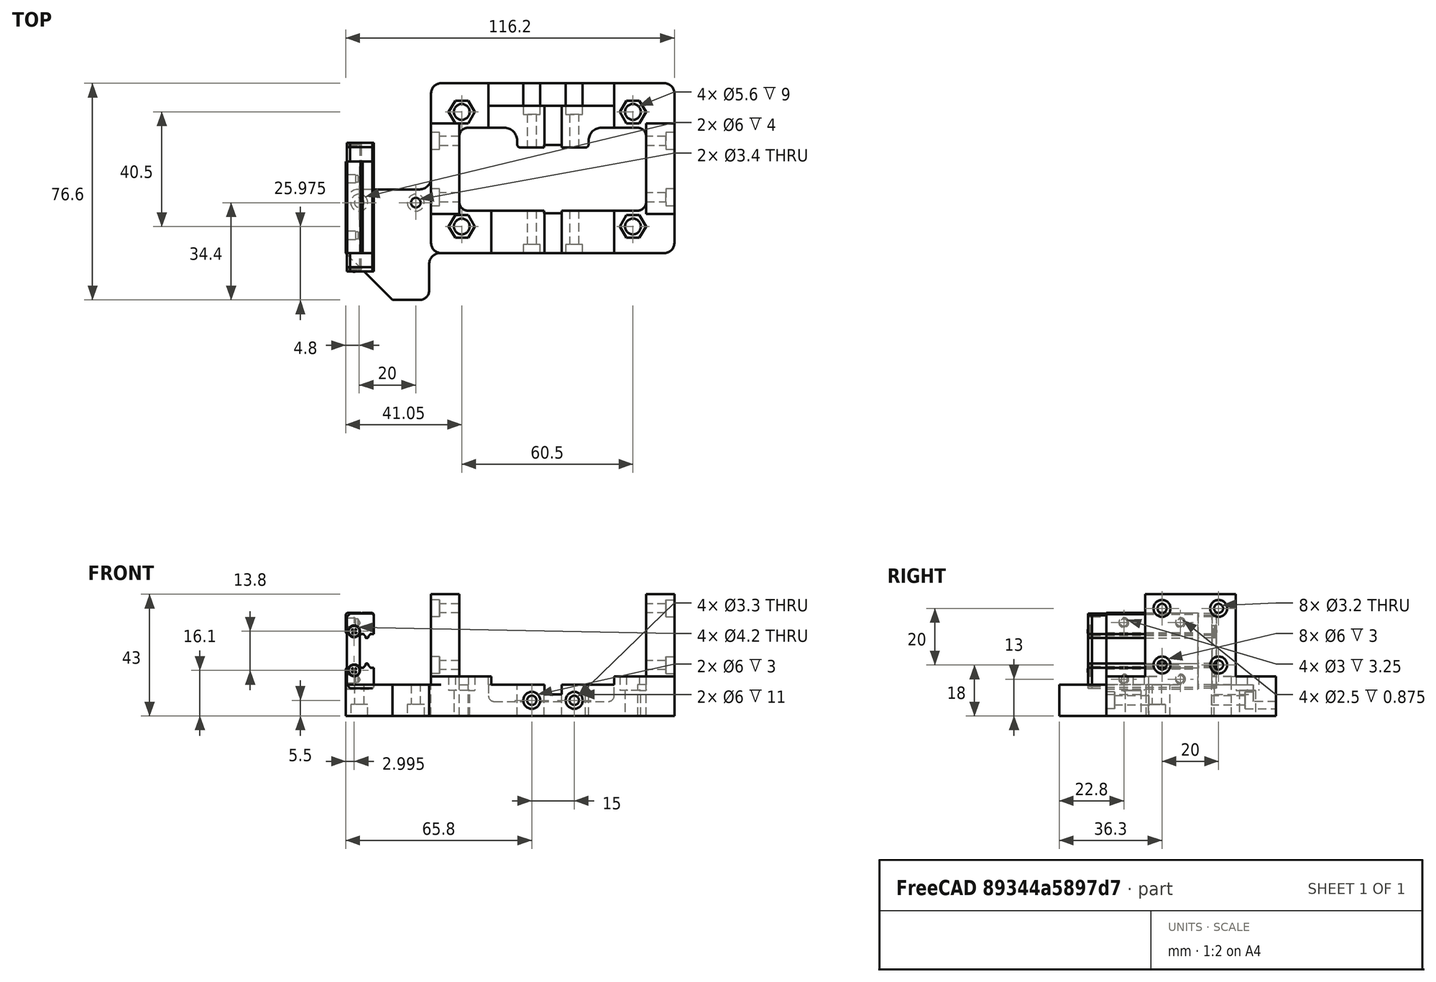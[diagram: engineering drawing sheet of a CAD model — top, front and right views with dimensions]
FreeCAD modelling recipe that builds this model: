
FCSTD DOCUMENT  (FreeCAD 0.19R24291 (Git))
Label: Carriage Mount
License: All rights reserved
LicenseURL: http://en.wikipedia.org/wiki/All_rights_reserved
objects: Sketcher::SketchObject×13, PartDesign::Pocket×10, Part::Feature×9, PartDesign::Pad×3, Mesh::Feature×2, App::Part×1, PartDesign::Body×1, Part::Fillet×1
note: 50 computed .brp shape members not serialized (recipe doc carries the construction recipe); baked Part::Feature solids carry a one-line shape summary decoded from their .brp

FEATURE [Mesh::Feature] y_axis_bed_carriage
  Placement = pos=(-82,-78.3,0) rot=(0,0,1;0rad)
FEATURE [Mesh::Feature] _a__y_belt_clip_x2  label="[a]_y_belt_clip_x2"
  Placement = pos=(-67,-7,115.5) rot=(1,0,0;4.71239rad)
FEATURE [Part::Feature] Part__Feature122  label="MGN12H, LINEAR GUIDE BLOCK v008"
  Placement = pos=(-22.7,16.2,23) rot=(0.57735,-0.57735,0.57735;2.0944rad)
  shape: bbox 4.316 x 1.614 x 4.52 mm, 16 faces (baked)
FEATURE [Part::Feature] Part__Feature121  label="MGN12H, LINEAR GUIDE BLOCK v007"
  Placement = pos=(-22.7,16.2,23) rot=(0.57735,-0.57735,0.57735;2.0944rad)
  shape: bbox 4.36 x 1.614 x 4.223 mm, 16 faces (baked)
FEATURE [Part::Feature] Part__Feature115  label="MGN12H, LINEAR GUIDE BLOCK v1"
  Placement = pos=(-22.7,16.2,23) rot=(0.57735,-0.57735,0.57735;2.0944rad)
  shape: bbox 10 x 32.4 x 27 mm, 66 faces (baked)
FEATURE [Part::Feature] Part__Feature123  label="MGN12H, LINEAR GUIDE BLOCK v009"
  Placement = pos=(-22.7,16.2,23) rot=(0.57735,-0.57735,0.57735;2.0944rad)
  shape: bbox 4.36 x 1.614 x 4.223 mm, 16 faces (baked)
FEATURE [Part::Feature] Part__Feature119  label="MGN12H, LINEAR GUIDE BLOCK v005"
  Placement = pos=(-22.7,16.2,23) rot=(0.57735,-0.57735,0.57735;2.0944rad)
  shape: bbox 9.6 x 1.5 x 26.4 mm, 42 faces (baked)
FEATURE [Part::Feature] Part__Feature120  label="MGN12H, LINEAR GUIDE BLOCK v006"
  Placement = pos=(-22.7,16.2,23) rot=(0.57735,-0.57735,0.57735;2.0944rad)
  shape: bbox 4.316 x 1.614 x 4.52 mm, 16 faces (baked)
FEATURE [Part::Feature] Part__Feature118  label="MGN12H, LINEAR GUIDE BLOCK v004"
  Placement = pos=(-22.7,16.2,23) rot=(0.57735,-0.57735,0.57735;2.0944rad)
  shape: bbox 9.6 x 1.5 x 26.4 mm, 42 faces (baked)
FEATURE [Part::Feature] Part__Feature116  label="MGN12H, LINEAR GUIDE BLOCK v002"
  Placement = pos=(-22.7,16.2,23) rot=(0.57735,-0.57735,0.57735;2.0944rad)
  shape: bbox 9.6 x 5 x 26.4 mm, 40 faces (baked)
FEATURE [Part::Feature] Part__Feature117  label="MGN12H, LINEAR GUIDE BLOCK v003"
  Placement = pos=(-22.7,16.2,23) rot=(0.57735,-0.57735,0.57735;2.0944rad)
  shape: bbox 9.6 x 5 x 26.4 mm, 40 faces (baked)
FEATURE [App::Part] MGN12H__LINEAR_GUIDE_BLOCK_v1  label="MGN12H, LINEAR GUIDE BLOCK v010"
  Group = -> [Part__Feature115,Part__Feature116,Part__Feature117,Part__Feature118,Part__Feature119,Part__Feature120,Part__Feature121,Part__Feature122,Part__Feature123]
  Origin = -> Origin028
  Placement = pos=(40.5,13.5,5) rot=(0,0,1;0rad)
FEATURE [Sketcher::SketchObject] Sketch
  FullyConstrained = true
  MapMode = 5
  Support = -> [XY_Plane]
  sketch-geometry (49):
    g0: LineSegment StartX=3.3 StartY=0 StartZ=0 EndX=82.5 EndY=0 EndZ=0
    g1: LineSegment StartX=86 StartY=3.5 StartZ=0 EndX=86 EndY=56.5 EndZ=0
    g2: LineSegment StartX=82.5 StartY=60 StartZ=0 EndX=3.5 EndY=60 EndZ=0
    g3: LineSegment StartX=0 StartY=56.5 StartZ=0 EndX=0 EndY=26.5 EndZ=0
    g4: ArcOfCircle CenterX=82.5 CenterY=3.5 CenterZ=0 NormalX=0 NormalY=0 NormalZ=1 AngleXU=0 Radius=3.5 StartAngle=4.71239 EndAngle=6.28319
    g5: ArcOfCircle CenterX=82.5 CenterY=56.5 CenterZ=0 NormalX=0 NormalY=0 NormalZ=1 AngleXU=0 Radius=3.5 StartAngle=7e-16 EndAngle=1.5708
    g6: ArcOfCircle CenterX=3.5 CenterY=56.5 CenterZ=0 NormalX=0 NormalY=0 NormalZ=1 AngleXU=0 Radius=3.5 StartAngle=1.5708 EndAngle=3.14159
    g7: ArcOfCircle CenterX=3.3 CenterY=-4 CenterZ=0 NormalX=0 NormalY=0 NormalZ=1 AngleXU=0 Radius=4 StartAngle=1.5708 EndAngle=3.14159
    g8: LineSegment StartX=-4 StartY=22.5 StartZ=0 EndX=-25.6 EndY=22.5 EndZ=0
    g9: LineSegment StartX=-30.2 StartY=17.9 StartZ=0 EndX=-30.2 EndY=0 EndZ=0
    g10: LineSegment StartX=-30.2 StartY=0 StartZ=0 EndX=-13.6 EndY=-16.6 EndZ=0
    g11: LineSegment StartX=-13.6 StartY=-16.6 StartZ=0 EndX=-4 EndY=-16.6 EndZ=0
    g12: LineSegment StartX=-0.7 StartY=-13.3 StartZ=0 EndX=-0.7 EndY=-4 EndZ=0
    g13: ArcOfCircle CenterX=-4 CenterY=-13.3 CenterZ=0 NormalX=0 NormalY=0 NormalZ=1 AngleXU=0 Radius=3.3 StartAngle=4.71239 EndAngle=6.28319
    g14: ArcOfCircle CenterX=-4 CenterY=26.5 CenterZ=0 NormalX=0 NormalY=0 NormalZ=1 AngleXU=0 Radius=4 StartAngle=4.71239 EndAngle=6.28319
    g15: ArcOfCircle CenterX=-25.6 CenterY=17.9 CenterZ=0 NormalX=0 NormalY=0 NormalZ=1 AngleXU=0 Radius=4.6 StartAngle=1.5708 EndAngle=3.14159
    g16: Circle CenterX=-25.4 CenterY=17.8 CenterZ=0 NormalX=0 NormalY=0 NormalZ=1 AngleXU=0 Radius=1.7
    g17: Circle CenterX=-5.4 CenterY=17.8 CenterZ=0 NormalX=0 NormalY=0 NormalZ=1 AngleXU=0 Radius=1.7
    g18: Circle CenterX=10.85 CenterY=9.375 CenterZ=0 NormalX=0 NormalY=0 NormalZ=1 AngleXU=0 Radius=2.8
    g19: Circle CenterX=10.85 CenterY=49.875 CenterZ=0 NormalX=0 NormalY=0 NormalZ=1 AngleXU=0 Radius=2.8
    g20: LineSegment StartX=10.85 StartY=9.375 StartZ=0 EndX=10.85 EndY=49.875 EndZ=0
    g21: Circle CenterX=71.35 CenterY=9.375 CenterZ=0 NormalX=0 NormalY=0 NormalZ=1 AngleXU=0 Radius=2.8
    g22: LineSegment StartX=10.85 StartY=9.375 StartZ=0 EndX=71.35 EndY=9.375 EndZ=0
    g23: Circle CenterX=71.35 CenterY=49.875 CenterZ=0 NormalX=0 NormalY=0 NormalZ=1 AngleXU=0 Radius=2.8
    g24: LineSegment StartX=71.35 StartY=9.375 StartZ=0 EndX=71.35 EndY=49.875 EndZ=0
    g25: LineSegment StartX=13 StartY=44.275 StartZ=0 EndX=25.9042 EndY=44.275 EndZ=0
    g26: LineSegment StartX=76 StartY=41.2768 StartZ=0 EndX=76 EndY=17.975 EndZ=0
    g27: LineSegment StartX=73 StartY=14.975 StartZ=0 EndX=46.2 EndY=14.975 EndZ=0
    g28: LineSegment StartX=10 StartY=17.9683 StartZ=0 EndX=10 EndY=41.275 EndZ=0
    g29: ArcOfCircle CenterX=13 CenterY=17.9683 CenterZ=0 NormalX=0 NormalY=0 NormalZ=1 AngleXU=0 Radius=3 StartAngle=3.14159 EndAngle=4.77911
    g30: ArcOfCircle CenterX=73 CenterY=17.975 CenterZ=0 NormalX=0 NormalY=0 NormalZ=1 AngleXU=0 Radius=3 StartAngle=4.71239 EndAngle=6.28319
    g31: ArcOfCircle CenterX=13 CenterY=41.275 CenterZ=0 NormalX=0 NormalY=0 NormalZ=1 AngleXU=0 Radius=3 StartAngle=1.5708 EndAngle=3.14159
    g32: ArcOfCircle CenterX=73 CenterY=41.2768 CenterZ=0 NormalX=0 NormalY=0 NormalZ=1 AngleXU=0 Radius=3 StartAngle=1e-15 EndAngle=1.53606
    g33: LineSegment StartX=30.4 StartY=39.7792 StartZ=0 EndX=30.4 EndY=38.475 EndZ=0
    g34: LineSegment StartX=31.6 StartY=37.275 StartZ=0 EndX=40 EndY=37.275 EndZ=0
    g35: LineSegment StartX=55.7 StartY=38.4708 StartZ=0 EndX=55.7 EndY=39.775 EndZ=0
    g36: LineSegment StartX=60.2 StartY=44.275 StartZ=0 EndX=73.1042 EndY=44.275 EndZ=0
    g37: ArcOfCircle CenterX=25.9042 CenterY=39.7792 CenterZ=0 NormalX=0 NormalY=0 NormalZ=1 AngleXU=0 Radius=4.49583 StartAngle=1e-16 EndAngle=1.5708
    g38: ArcOfCircle CenterX=60.2 CenterY=39.775 CenterZ=0 NormalX=0 NormalY=0 NormalZ=1 AngleXU=0 Radius=4.5 StartAngle=1.5708 EndAngle=3.14159
    g39: ArcOfCircle CenterX=54.5 CenterY=38.4708 CenterZ=0 NormalX=0 NormalY=0 NormalZ=1 AngleXU=0 Radius=1.2 StartAngle=4.79582 EndAngle=6.28319
    g40: ArcOfCircle CenterX=31.6 CenterY=38.475 CenterZ=0 NormalX=0 NormalY=0 NormalZ=1 AngleXU=0 Radius=1.2 StartAngle=3.14159 EndAngle=4.71239
    g41: LineSegment StartX=40 StartY=37.275 StartZ=0 EndX=40 EndY=38.175 EndZ=0
    g42: LineSegment StartX=40 StartY=38.175 StartZ=0 EndX=46.2 EndY=38.175 EndZ=0
    g43: LineSegment StartX=46.2 StartY=38.175 StartZ=0 EndX=46.2 EndY=37.275 EndZ=0
    g44: LineSegment StartX=46.2 StartY=37.275 StartZ=0 EndX=54.6 EndY=37.275 EndZ=0
    g45: LineSegment StartX=40 StartY=14.975 StartZ=0 EndX=40 EndY=14.075 EndZ=0
    g46: LineSegment StartX=40 StartY=14.075 StartZ=0 EndX=46.2 EndY=14.075 EndZ=0
    g47: LineSegment StartX=46.2 StartY=14.075 StartZ=0 EndX=46.2 EndY=14.975 EndZ=0
    g48: LineSegment StartX=40 StartY=14.975 StartZ=0 EndX=13.2 EndY=14.975 EndZ=0
  constraints (131):
    c: Horizontal(g0)
    c: Horizontal(g2)
    c: Vertical(g1)
    c: Vertical(g3)
    c: Tangent(g0,g4) = -1.5708
    c: Tangent(g1,g4) = -1.5708
    c: Tangent(g1,g5) = -1.5708
    c: Tangent(g2,g5) = -1.5708
    c: Tangent(g3,g6) = -1.5708
    c: Tangent(g2,g6) = -1.5708
    c: PointOnObject(g0,g-1)
    c: DistanceY(g-1,g2) = 60
    c: Radius(g6) = 3.5
    c: Coincident(g7,g0)
    c: Horizontal(g8)
    c: PointOnObject(g9,g-1)
    c: Vertical(g9)
    c: Coincident(g9,g10)
    c: Coincident(g10,g11)
    c: Horizontal(g11)
    c: Coincident(g12,g7)
    c: Vertical(g12)
    c: Tangent(g11,g13) = -1.5708
    c: Tangent(g12,g13) = -1.5708
    c: Tangent(g8,g14) = 1.5708
    c: Tangent(g3,g14) = 1.5708
    c: Tangent(g9,g15) = -1.5708
    c: Tangent(g8,g15) = -1.5708
    c: PointOnObject(g3,g-2)
    c: Equal(g6,g5)
    c: Equal(g5,g4)
    c: Angle(g7) = 1.5708
    c: DistanceY(g-1,g8) = 22.5
    c: DistanceX(g9,g-1) = 30.2
    c: DistanceY(g11,g-1) = 16.6
    c: DistanceX(g7,g-1) = 0.7
    c: Distance(g12) = 9.3
    c: Radius(g7) = 4
    c: DistanceX(g11,g11) = 9.6
    c: Radius(g15) = 4.6
    c: Radius(g14) = 4
    c: DistanceX(g3,g1) = 86
    c: DistanceY(g7,g-1) = 4
    c: Radius(g16) = 1.7
    c: Equal(g16,g17) = 1.7
    c: Horizontal(g16,g17)
    c: DistanceX(g17,g-1) = 5.4
    c: DistanceX(g16,g17) = 20
    c: DistanceY(g-1,g17) = 17.8
    c: Radius(g18) = 2.8
    c: DistanceX(g-1,g18) = 10.85
    c: DistanceY(g-1,g18) = 9.375
    c: Radius(g19) = 2.8
    c: Coincident(g18,g20)
    c: Coincident(g19,g20)
    c: Distance(g20) = 40.5
    c: Angle(g20) = 1.5708
    c: Radius(g21) = 2.8
    c: Coincident(g18,g22)
    c: Coincident(g21,g22)
    c: Distance(g22) = 60.5
    c: Perpendicular(g22,g20)
    c: Radius(g23) = 2.8
    c: Coincident(g21,g24)
    c: Coincident(g23,g24)
    c: Equal(g20,g24)
    c: Parallel(g24,g20)
    c: Horizontal(g25)
    c: Horizontal(g27)
    c: Vertical(g26)
    c: Vertical(g28)
    c: Tangent(g28,g29) = 1.5708
    c: Coincident(g48,g29) = 1.5708
    c: Tangent(g27,g30) = 1.5708
    c: Tangent(g26,g30) = 1.5708
    c: Tangent(g28,g31) = 1.5708
    c: Tangent(g25,g31) = 1.5708
    c: Coincident(g36,g32) = 1.5708
    c: Tangent(g26,g32) = 1.5708
    c: Equal(g29,g31)
    c: Equal(g31,g32)
    c: Equal(g32,g30)
    c: Radius(g29) = 3
    c: DistanceX(g-1,g28) = 10
    c: DistanceX(g26,g1) = 10
    c: DistanceY(g18,g48) = 5.6
    c: DistanceY(g25,g19) = 5.6
    c: Vertical(g33)
    c: Horizontal(g34)
    c: Vertical(g35)
    c: Tangent(g25,g36)
    c: Tangent(g25,g37) = 1.5708
    c: Tangent(g33,g37) = 1.5708
    c: Tangent(g35,g38) = 1.5708
    c: Tangent(g36,g38) = 1.5708
    c: Coincident(g44,g39) = -1.5708
    c: Tangent(g35,g39) = -1.5708
    c: Tangent(g33,g40) = -1.5708
    c: Tangent(g34,g40) = -1.5708
    c: Equal(g40,g39)
    c: DistanceY(g34,g25) = 7
    c: DistanceX(g28,g33) = 20.4
    c: DistanceX(g33,g35) = 25.3
    c: Radius(g40) = 1.2
    c: Equal(g33,g35)
    c: Equal(g25,g36)
    c: Radius(g38) = 4.5
    c: Vertical(g41)
    c: Coincident(g41,g42)
    c: Horizontal(g42)
    c: Coincident(g42,g43)
    c: Vertical(g43)
    c: Coincident(g34,g41)
    c: Coincident(g44,g43)
    c: Tangent(g34,g44)
    c: Equal(g34,g44)
    c: DistanceX(g42,g42) = 6.2
    c: DistanceX(g34,g34) = 8.4
    c: DistanceY(g43,g43) = 0.9
    c: Coincident(g45,g46)
    c: Horizontal(g46)
    c: Coincident(g46,g47)
    c: Vertical(g47)
    c: Vertical(g45)
    c: Equal(g42,g46)
    c: Equal(g43,g47)
    c: Coincident(g27,g47)
    c: Coincident(g48,g45)
    c: Tangent(g27,g48)
    c: Equal(g48,g27)
    c: DistanceX(g48,g48) = 26.8
FEATURE [PartDesign::Pad] Pad
  Direction = (1,1,1)
  Length = 11
  Length2 = 100
  Profile = -> Sketch
  Type = 0
FEATURE [Sketcher::SketchObject] Sketch001
  ExternalGeometry = -> [Pad]
  FullyConstrained = true
  MapMode = 5
  Placement = pos=(0,0,11) rot=(0,0,1;0rad)
  Support = -> [Pad]
  sketch-geometry (24):
    g0: LineSegment StartX=3.5 StartY=0 StartZ=0 EndX=21.3 EndY=0 EndZ=0
    g1: LineSegment StartX=21.3 StartY=0 StartZ=0 EndX=21.3 EndY=14.975 EndZ=0
    g2: LineSegment StartX=21.3 StartY=14.975 StartZ=0 EndX=12.9933 EndY=14.975 EndZ=0
    g3: LineSegment StartX=10 StartY=17.9683 StartZ=0 EndX=10 EndY=41.275 EndZ=0
    g4: LineSegment StartX=20.3 StartY=44.275 StartZ=0 EndX=20.3 EndY=60 EndZ=0
    g5: LineSegment StartX=20.3 StartY=60 StartZ=0 EndX=3.5 EndY=60 EndZ=0
    g6: LineSegment StartX=0 StartY=56.5 StartZ=0 EndX=0 EndY=3.5 EndZ=0
    g7: ArcOfCircle CenterX=12.9933 CenterY=17.9683 CenterZ=0 NormalX=0 NormalY=0 NormalZ=1 AngleXU=0 Radius=2.99333 StartAngle=3.14159 EndAngle=4.71239
    g8: ArcOfCircle CenterX=13 CenterY=41.275 CenterZ=0 NormalX=0 NormalY=0 NormalZ=1 AngleXU=0 Radius=3 StartAngle=1.5708 EndAngle=3.14159
    g9: ArcOfCircle CenterX=3.5 CenterY=56.5 CenterZ=0 NormalX=0 NormalY=0 NormalZ=1 AngleXU=0 Radius=3.5 StartAngle=1.5708 EndAngle=3.14159
    g10: LineSegment StartX=13 StartY=44.275 StartZ=0 EndX=20.3 EndY=44.275 EndZ=0
    g11: ArcOfCircle CenterX=3.5 CenterY=3.5 CenterZ=0 NormalX=0 NormalY=0 NormalZ=1 AngleXU=0 Radius=3.5 StartAngle=3.14159 EndAngle=4.71239
    g12: LineSegment StartX=64.7 StartY=0 StartZ=0 EndX=64.7 EndY=14.975 EndZ=0
    g13: LineSegment StartX=64.7 StartY=14.975 StartZ=0 EndX=73 EndY=14.975 EndZ=0
    g14: LineSegment StartX=76 StartY=17.975 StartZ=0 EndX=76 EndY=41.2768 EndZ=0
    g15: LineSegment StartX=73.0018 StartY=44.275 StartZ=0 EndX=64.7018 EndY=44.275 EndZ=0
    g16: LineSegment StartX=64.7018 StartY=44.275 StartZ=0 EndX=64.7018 EndY=60 EndZ=0
    g17: LineSegment StartX=64.7018 StartY=60 StartZ=0 EndX=82.5 EndY=60 EndZ=0
    g18: LineSegment StartX=86 StartY=56.5 StartZ=0 EndX=86 EndY=3.5 EndZ=0
    g19: LineSegment StartX=82.5 StartY=0 StartZ=0 EndX=64.7 EndY=0 EndZ=0
    g20: ArcOfCircle CenterX=73 CenterY=17.975 CenterZ=0 NormalX=0 NormalY=0 NormalZ=1 AngleXU=0 Radius=3 StartAngle=4.71239 EndAngle=6.28319
    g21: ArcOfCircle CenterX=73.0018 CenterY=41.2768 CenterZ=0 NormalX=0 NormalY=0 NormalZ=1 AngleXU=0 Radius=2.99819 StartAngle=1.1e-15 EndAngle=1.5708
    g22: ArcOfCircle CenterX=82.5 CenterY=56.5 CenterZ=0 NormalX=0 NormalY=0 NormalZ=1 AngleXU=0 Radius=3.5 StartAngle=0 EndAngle=1.5708
    g23: ArcOfCircle CenterX=82.5 CenterY=3.5 CenterZ=0 NormalX=0 NormalY=0 NormalZ=1 AngleXU=0 Radius=3.5 StartAngle=4.71239 EndAngle=6.28319
  constraints (56):
    c: PointOnObject(g0,g-1)
    c: Coincident(g0,g1)
    c: PointOnObject(g1,g-3)
    c: Vertical(g1)
    c: Coincident(g1,g2)
    c: Horizontal(g2)
    c: PointOnObject(g4,g-6)
    c: Vertical(g4)
    c: Coincident(g4,g5)
    c: Tangent(g3,g7) = 1.5708
    c: Tangent(g2,g7) = 1.5708
    c: Coincident(g3,g-4)
    c: DistanceX(g-1,g0) = 21.3
    c: Tangent(g3,g8) = 1.5708
    c: Coincident(g-5,g8) = 1.5708
    c: Tangent(g6,g9) = -1.5708
    c: Tangent(g5,g9) = -1.5708
    c: Coincident(g10,g8)
    c: Coincident(g10,g4)
    c: Horizontal(g10)
    c: DistanceX(g6,g4) = 20.3
    c: Coincident(g5,g-6)
    c: PointOnObject(g6,g-2)
    c: Coincident(g3,g-4)
    c: Tangent(g6,g11) = -1.5708
    c: Tangent(g0,g11) = -1.5708
    c: Radius(g11) = 3.5
    c: PointOnObject(g6,g-2)
    c: PointOnObject(g0,g-1)
    c: PointOnObject(g12,g-1)
    c: Vertical(g12)
    c: Coincident(g12,g13)
    c: Horizontal(g15)
    c: Coincident(g15,g16)
    c: PointOnObject(g16,g-6)
    c: Vertical(g16)
    c: Coincident(g16,g17)
    c: Vertical(g18)
    c: Coincident(g19,g12)
    c: Tangent(g13,g20) = -1.5708
    c: Tangent(g14,g20) = -1.5708
    c: Tangent(g15,g21) = -1.5708
    c: Tangent(g14,g21) = -1.5708
    c: Tangent(g17,g22) = 1.5708
    c: Tangent(g18,g22) = 1.5708
    c: Tangent(g19,g23) = 1.5708
    c: Tangent(g18,g23) = 1.5708
    c: Coincident(g18,g-10)
    c: DistanceX(g12,g18) = 21.3
    c: Horizontal(g19)
    c: Coincident(g13,g-8)
    c: Coincident(g14,g-9)
    c: Coincident(g14,g-9)
    c: PointOnObject(g15,g-7)
    c: Equal(g13,g15)
    c: Coincident(g17,g-6)
FEATURE [PartDesign::Pad] Pad001
  BaseFeature = -> Pad
  Direction = (1,1,1)
  Length = 3
  Length2 = 100
  Profile = -> Sketch001
  Type = 0
FEATURE [Sketcher::SketchObject] Sketch002
  ExternalGeometry = -> [Pad]
  FullyConstrained = true
  MapMode = 5
  Placement = pos=(0,0,14) rot=(0,0,1;0rad)
  Support = -> [Pad001]
  sketch-geometry (28):
    g0: LineSegment StartX=13.1594 StartY=5.375 StartZ=0 EndX=15.4688 EndY=9.375 EndZ=0
    g1: LineSegment StartX=15.4688 StartY=9.375 StartZ=0 EndX=13.1594 EndY=13.375 EndZ=0
    g2: LineSegment StartX=13.1594 StartY=13.375 StartZ=0 EndX=8.5406 EndY=13.375 EndZ=0
    g3: LineSegment StartX=8.5406 StartY=13.375 StartZ=0 EndX=6.2312 EndY=9.375 EndZ=0
    g4: LineSegment StartX=6.2312 StartY=9.375 StartZ=0 EndX=8.5406 EndY=5.375 EndZ=0
    g5: LineSegment StartX=8.5406 StartY=5.375 StartZ=0 EndX=13.1594 EndY=5.375 EndZ=0
    g6: Circle CenterX=10.85 CenterY=9.375 CenterZ=0 NormalX=0 NormalY=0 NormalZ=1 AngleXU=0 Radius=4.6188
    g7: LineSegment StartX=13.1594 StartY=45.875 StartZ=0 EndX=15.4688 EndY=49.875 EndZ=0
    g8: LineSegment StartX=15.4688 StartY=49.875 StartZ=0 EndX=13.1594 EndY=53.875 EndZ=0
    g9: LineSegment StartX=13.1594 StartY=53.875 StartZ=0 EndX=8.5406 EndY=53.875 EndZ=0
    g10: LineSegment StartX=8.5406 StartY=53.875 StartZ=0 EndX=6.2312 EndY=49.875 EndZ=0
    g11: LineSegment StartX=6.2312 StartY=49.875 StartZ=0 EndX=8.5406 EndY=45.875 EndZ=0
    g12: LineSegment StartX=8.5406 StartY=45.875 StartZ=0 EndX=13.1594 EndY=45.875 EndZ=0
    g13: Circle CenterX=10.85 CenterY=49.875 CenterZ=0 NormalX=0 NormalY=0 NormalZ=1 AngleXU=0 Radius=4.6188
    g14: LineSegment StartX=73.6594 StartY=45.875 StartZ=0 EndX=75.9688 EndY=49.875 EndZ=0
    g15: LineSegment StartX=75.9688 StartY=49.875 StartZ=0 EndX=73.6594 EndY=53.875 EndZ=0
    g16: LineSegment StartX=73.6594 StartY=53.875 StartZ=0 EndX=69.0406 EndY=53.875 EndZ=0
    g17: LineSegment StartX=69.0406 StartY=53.875 StartZ=0 EndX=66.7312 EndY=49.875 EndZ=0
    g18: LineSegment StartX=66.7312 StartY=49.875 StartZ=0 EndX=69.0406 EndY=45.875 EndZ=0
    g19: LineSegment StartX=69.0406 StartY=45.875 StartZ=0 EndX=73.6594 EndY=45.875 EndZ=0
    g20: Circle CenterX=71.35 CenterY=49.875 CenterZ=0 NormalX=0 NormalY=0 NormalZ=1 AngleXU=0 Radius=4.6188
    g21: LineSegment StartX=73.6594 StartY=5.375 StartZ=0 EndX=75.9688 EndY=9.375 EndZ=0
    g22: LineSegment StartX=75.9688 StartY=9.375 StartZ=0 EndX=73.6594 EndY=13.375 EndZ=0
    g23: LineSegment StartX=73.6594 StartY=13.375 StartZ=0 EndX=69.0406 EndY=13.375 EndZ=0
    g24: LineSegment StartX=69.0406 StartY=13.375 StartZ=0 EndX=66.7312 EndY=9.375 EndZ=0
    g25: LineSegment StartX=66.7312 StartY=9.375 StartZ=0 EndX=69.0406 EndY=5.375 EndZ=0
    g26: LineSegment StartX=69.0406 StartY=5.375 StartZ=0 EndX=73.6594 EndY=5.375 EndZ=0
    g27: Circle CenterX=71.35 CenterY=9.375 CenterZ=0 NormalX=0 NormalY=0 NormalZ=1 AngleXU=0 Radius=4.6188
  constraints (64):
    c: Coincident(g0,g1)
    c: Coincident(g1,g2)
    c: Coincident(g2,g3)
    c: Coincident(g3,g4)
    c: Coincident(g4,g5)
    c: Coincident(g5,g0)
    c: Equal(g0, g1-g5) x5
    c: PointOnObject(g0,g6)
    c: PointOnObject(g1,g6)
    c: PointOnObject(g2,g6)
    c: PointOnObject(g3,g6)
    c: PointOnObject(g4,g6)
    c: PointOnObject(g5,g6)
    c: Coincident(g6,g-3)
    c: Horizontal(g2)
    c: DistanceY(g4,g2) = 8
    c: Coincident(g7,g8)
    c: Coincident(g8,g9)
    c: Coincident(g9,g10)
    c: Coincident(g10,g11)
    c: Coincident(g11,g12)
    c: Coincident(g12,g7)
    c: Equal(g7, g8-g12) x5
    c: PointOnObject(g7,g13)
    c: PointOnObject(g8,g13)
    c: PointOnObject(g9,g13)
    c: PointOnObject(g10,g13)
    c: PointOnObject(g11,g13)
    c: PointOnObject(g12,g13)
    c: Coincident(g13,g-4)
    c: Coincident(g14,g15)
    c: Coincident(g15,g16)
    c: Coincident(g16,g17)
    c: Coincident(g17,g18)
    c: Coincident(g18,g19)
    c: Coincident(g19,g14)
    c: Equal(g14, g15-g19) x5
    c: PointOnObject(g14,g20)
    c: PointOnObject(g15,g20)
    c: PointOnObject(g16,g20)
    c: PointOnObject(g17,g20)
    c: PointOnObject(g18,g20)
    c: PointOnObject(g19,g20)
    c: Coincident(g20,g-5)
    c: Coincident(g21,g22)
    c: Coincident(g22,g23)
    c: Coincident(g23,g24)
    c: Coincident(g24,g25)
    c: Coincident(g25,g26)
    c: Coincident(g26,g21)
    c: Equal(g21, g22-g26) x5
    c: PointOnObject(g21,g27)
    c: PointOnObject(g22,g27)
    c: PointOnObject(g23,g27)
    c: PointOnObject(g24,g27)
    c: PointOnObject(g25,g27)
    c: PointOnObject(g26,g27)
    c: Coincident(g27,g-6)
    c: Horizontal(g23)
    c: DistanceY(g25,g23) = 8
    c: Horizontal(g9)
    c: Horizontal(g16)
    c: DistanceY(g11,g9) = 8
    c: DistanceY(g18,g16) = 8
FEATURE [PartDesign::Pocket] Pocket
  BaseFeature = -> Pad001
  Length = 5
  Length2 = 100
  Profile = -> Sketch002
  Type = 0
FEATURE [Sketcher::SketchObject] Sketch003
  ExternalGeometry = -> [Pocket]
  FullyConstrained = true
  MapMode = 5
  Placement = pos=(0,0,0) rot=(1,0,0;1.5708rad)
  Support = -> [Pocket]
  sketch-geometry (2):
    g0: Circle CenterX=35.6 CenterY=5.5 CenterZ=0 NormalX=0 NormalY=0 NormalZ=1 AngleXU=0 Radius=1.65
    g1: Circle CenterX=50.6 CenterY=5.5 CenterZ=0 NormalX=0 NormalY=0 NormalZ=1 AngleXU=0 Radius=1.65
  constraints (6):
    c: Radius(g0) = 1.65
    c: Equal(g0,g1)
    c: DistanceX(g0,g1) = 15
    c: DistanceX(g-1,g0) = 35.6
    c: DistanceY(g-1,g0) = 5.5
    c: Horizontal(g0,g1)
FEATURE [PartDesign::Pocket] Pocket001
  BaseFeature = -> Pocket
  Length = 60
  Length2 = 100
  Profile = -> Sketch003
  Type = 0
FEATURE [Sketcher::SketchObject] Sketch004
  ExternalGeometry = -> [Pocket001]
  FullyConstrained = true
  MapMode = 5
  Placement = pos=(0,0,0) rot=(1,0,0;1.5708rad)
  Support = -> [Pocket001]
  sketch-geometry (2):
    g0: Circle CenterX=35.6 CenterY=5.5 CenterZ=0 NormalX=0 NormalY=0 NormalZ=1 AngleXU=0 Radius=3
    g1: Circle CenterX=50.6 CenterY=5.5 CenterZ=0 NormalX=0 NormalY=0 NormalZ=1 AngleXU=0 Radius=3
  constraints (4):
    c: Radius(g0) = 3
    c: Equal(g0,g1)
    c: Coincident(g1,g-4)
    c: Coincident(g0,g-3)
FEATURE [PartDesign::Pocket] Pocket002
  BaseFeature = -> Pocket001
  Length = 3
  Length2 = 100
  Profile = -> Sketch004
  Type = 0
FEATURE [Sketcher::SketchObject] Sketch005
  ExternalGeometry = -> [Pocket002]
  FullyConstrained = true
  MapMode = 5
  Placement = pos=(0,0,0) rot=(1,0,0;3.14159rad)
  Support = -> [Pocket002]
  sketch-geometry (2):
    g0: Circle CenterX=-25.4 CenterY=-17.8 CenterZ=0 NormalX=0 NormalY=0 NormalZ=1 AngleXU=0 Radius=3
    g1: Circle CenterX=-5.4 CenterY=-17.8 CenterZ=0 NormalX=0 NormalY=0 NormalZ=1 AngleXU=0 Radius=3
  constraints (4):
    c: Coincident(g0,g-3)
    c: Coincident(g1,g-4)
    c: Equal(g0,g1)
    c: Radius(g0) = 3
FEATURE [PartDesign::Pocket] Pocket003  label="Belt Cutout"
  BaseFeature = -> Pocket002
  Length = 4
  Length2 = 100
  Profile = -> Sketch005
  Type = 0
FEATURE [Sketcher::SketchObject] Sketch006
  ExternalGeometry = -> [Pocket003]
  FullyConstrained = true
  MapMode = 5
  Placement = pos=(0,0,14) rot=(0,0,1;0rad)
  Support = -> [Pocket003]
  sketch-geometry (8):
    g0: LineSegment StartX=0 StartY=13.8 StartZ=0 EndX=10 EndY=13.8 EndZ=0
    g1: LineSegment StartX=10 StartY=13.8 StartZ=0 EndX=10 EndY=45.8 EndZ=0
    g2: LineSegment StartX=10 StartY=45.8 StartZ=0 EndX=0 EndY=45.8 EndZ=0
    g3: LineSegment StartX=0 StartY=45.8 StartZ=0 EndX=0 EndY=13.8 EndZ=0
    g4: LineSegment StartX=86 StartY=13.8 StartZ=0 EndX=76 EndY=13.8 EndZ=0
    g5: LineSegment StartX=76 StartY=13.8 StartZ=0 EndX=76 EndY=45.8 EndZ=0
    g6: LineSegment StartX=76 StartY=45.8 StartZ=0 EndX=86 EndY=45.8 EndZ=0
    g7: LineSegment StartX=86 StartY=45.8 StartZ=0 EndX=86 EndY=13.8 EndZ=0
  constraints (24):
    c: Coincident(g0,g1)
    c: Coincident(g1,g2)
    c: Coincident(g2,g3)
    c: Coincident(g3,g0)
    c: Horizontal(g0)
    c: Horizontal(g2)
    c: Vertical(g1)
    c: Vertical(g3)
    c: PointOnObject(g0,g-2)
    c: DistanceX(g2,g2) = 10
    c: DistanceY(g3,g3) = 32
    c: DistanceY(g-1,g0) = 13.8
    c: Coincident(g4,g5)
    c: Coincident(g5,g6)
    c: Coincident(g6,g7)
    c: Coincident(g7,g4)
    c: Horizontal(g4)
    c: Horizontal(g6)
    c: Vertical(g5)
    c: Vertical(g7)
    c: PointOnObject(g4,g-3)
    c: PointOnObject(g-4,g5)
    c: Equal(g3,g7)
    c: DistanceY(g-1,g4) = 13.8
FEATURE [PartDesign::Pad] Pad002  label="MGN12H Supports"
  BaseFeature = -> Pocket003
  Direction = (1,1,1)
  Length = 29
  Length2 = 100
  Profile = -> Sketch006
  Type = 0
FEATURE [Sketcher::SketchObject] Sketch007
  FullyConstrained = true
  MapMode = 5
  Placement = pos=(0,0,0) rot=(0.57735,-0.57735,-0.57735;2.0944rad)
  Support = -> [Pad002]
  sketch-geometry (7):
    g0: Circle CenterX=-39.7 CenterY=18 CenterZ=0 NormalX=0 NormalY=0 NormalZ=1 AngleXU=0 Radius=1.6
    g1: Circle CenterX=-39.7 CenterY=38 CenterZ=0 NormalX=0 NormalY=0 NormalZ=1 AngleXU=0 Radius=1.6
    g2: LineSegment StartX=-39.7 StartY=18 StartZ=0 EndX=-39.7 EndY=38 EndZ=0
    g3: Circle CenterX=-19.7 CenterY=18 CenterZ=0 NormalX=0 NormalY=0 NormalZ=1 AngleXU=0 Radius=1.6
    g4: LineSegment StartX=-39.7 StartY=18 StartZ=0 EndX=-19.7 EndY=18 EndZ=0
    g5: Circle CenterX=-19.7 CenterY=38 CenterZ=0 NormalX=0 NormalY=0 NormalZ=1 AngleXU=0 Radius=1.6
    g6: LineSegment StartX=-19.7 StartY=18 StartZ=0 EndX=-19.7 EndY=38 EndZ=0
  constraints (18):
    c: Radius(g0) = 1.6
    c: DistanceY(g-1,g0) = 18
    c: DistanceX(g0,g-1) = 39.7
    c: Radius(g1) = 1.6
    c: Coincident(g0,g2)
    c: Coincident(g1,g2)
    c: Distance(g2) = 20
    c: Angle(g2) = 1.5708
    c: Radius(g3) = 1.6
    c: Coincident(g0,g4)
    c: Coincident(g3,g4)
    c: Distance(g4) = 20
    c: Perpendicular(g4,g2)
    c: Radius(g5) = 1.6
    c: Coincident(g3,g6)
    c: Coincident(g5,g6)
    c: Equal(g2,g6)
    c: Parallel(g6,g2)
FEATURE [PartDesign::Pocket] Pocket004
  BaseFeature = -> Pad002
  Length = 90
  Length2 = 100
  Profile = -> Sketch007
  Type = 0
FEATURE [Sketcher::SketchObject] Sketch008
  ExternalGeometry = -> [Pocket004]
  FullyConstrained = true
  MapMode = 5
  Placement = pos=(0,0,0) rot=(0.57735,-0.57735,-0.57735;2.0944rad)
  Support = -> [Pocket004]
  sketch-geometry (4):
    g0: Circle CenterX=-39.7 CenterY=38 CenterZ=0 NormalX=0 NormalY=0 NormalZ=1 AngleXU=0 Radius=3
    g1: Circle CenterX=-39.7 CenterY=18 CenterZ=0 NormalX=0 NormalY=0 NormalZ=1 AngleXU=0 Radius=3
    g2: Circle CenterX=-19.7 CenterY=38 CenterZ=0 NormalX=0 NormalY=0 NormalZ=1 AngleXU=0 Radius=3
    g3: Circle CenterX=-19.7 CenterY=18 CenterZ=0 NormalX=0 NormalY=0 NormalZ=1 AngleXU=0 Radius=3
  constraints (8):
    c: Coincident(g0,g-3)
    c: Radius(g0) = 3
    c: Equal(g0,g1) = 3
    c: Coincident(g1,g-6)
    c: Equal(g0,g2) = 3
    c: Coincident(g2,g-4)
    c: Equal(g0,g3) = 3
    c: Coincident(g3,g-5)
FEATURE [PartDesign::Pocket] Pocket005
  BaseFeature = -> Pocket004
  Length = 3
  Length2 = 100
  Profile = -> Sketch008
  Type = 0
FEATURE [Sketcher::SketchObject] Sketch009
  ExternalGeometry = -> [Pocket005]
  FullyConstrained = true
  MapMode = 5
  Placement = pos=(86,0,0) rot=(0.57735,0.57735,0.57735;2.0944rad)
  Support = -> [Pocket005]
  sketch-geometry (4):
    g0: Circle CenterX=19.7 CenterY=38 CenterZ=0 NormalX=0 NormalY=0 NormalZ=1 AngleXU=0 Radius=3
    g1: Circle CenterX=19.7 CenterY=18 CenterZ=0 NormalX=0 NormalY=0 NormalZ=1 AngleXU=0 Radius=3
    g2: Circle CenterX=39.7 CenterY=38 CenterZ=0 NormalX=0 NormalY=0 NormalZ=1 AngleXU=0 Radius=3
    g3: Circle CenterX=39.7 CenterY=18 CenterZ=0 NormalX=0 NormalY=0 NormalZ=1 AngleXU=0 Radius=3
  constraints (8):
    c: Radius(g0) = 3
    c: Equal(g0,g1) = 3
    c: Equal(g0,g2) = 3
    c: Equal(g0,g3) = 3
    c: Coincident(g1,g-6)
    c: Coincident(g3,g-5)
    c: Coincident(g2,g-4)
    c: Coincident(g0,g-3)
FEATURE [PartDesign::Pocket] Pocket006
  BaseFeature = -> Pocket005
  Length = 3
  Length2 = 100
  Profile = -> Sketch009
  Type = 0
FEATURE [Sketcher::SketchObject] Sketch010
  ExternalGeometry = -> [Pocket006]
  FullyConstrained = true
  MapMode = 5
  Placement = pos=(0,0,0) rot=(1,0,0;1.5708rad)
  Support = -> [Pocket006]
  sketch-geometry (4):
    g0: LineSegment StartX=40.05 StartY=11 StartZ=0 EndX=46.15 EndY=11 EndZ=0
    g1: LineSegment StartX=46.15 StartY=11 StartZ=0 EndX=46.15 EndY=7.6 EndZ=0
    g2: LineSegment StartX=46.15 StartY=7.6 StartZ=0 EndX=40.05 EndY=7.6 EndZ=0
    g3: LineSegment StartX=40.05 StartY=7.6 StartZ=0 EndX=40.05 EndY=11 EndZ=0
  constraints (12):
    c: Coincident(g0,g1)
    c: Coincident(g1,g2)
    c: Coincident(g2,g3)
    c: Coincident(g3,g0)
    c: Horizontal(g0)
    c: Horizontal(g2)
    c: Vertical(g1)
    c: Vertical(g3)
    c: PointOnObject(g0,g-4)
    c: DistanceX(g0,g0) = 6.1
    c: DistanceX(g-3,g0) = 4.45
    c: DistanceY(g3,g3) = 3.4
FEATURE [PartDesign::Pocket] Pocket007
  BaseFeature = -> Pocket006
  Length = 60
  Length2 = 100
  Profile = -> Sketch010
  Type = 0
FEATURE [Sketcher::SketchObject] Sketch011
  ExternalGeometry = -> [Pocket007]
  FullyConstrained = true
  MapMode = 5
  Placement = pos=(0,60,0) rot=(0,0.707107,0.707107;3.14159rad)
  Support = -> [Pocket007]
  sketch-geometry (2):
    g0: Circle CenterX=-50.6 CenterY=5.5 CenterZ=0 NormalX=0 NormalY=0 NormalZ=1 AngleXU=0 Radius=3
    g1: Circle CenterX=-35.6 CenterY=5.5 CenterZ=0 NormalX=0 NormalY=0 NormalZ=1 AngleXU=0 Radius=3
  constraints (4):
    c: Coincident(g0,g-3)
    c: Coincident(g1,g-4)
    c: Radius(g0) = 3
    c: Equal(g0,g1)
FEATURE [PartDesign::Pocket] Pocket008
  BaseFeature = -> Pocket007
  Length = 11
  Length2 = 100
  Profile = -> Sketch011
  Type = 0
FEATURE [Sketcher::SketchObject] Sketch012
  ExternalGeometry = -> [Pocket008]
  FullyConstrained = true
  MapMode = 5
  Placement = pos=(0,60,0) rot=(0,0.707107,0.707107;3.14159rad)
  Support = -> [Pocket008]
  sketch-geometry (6):
    g0: LineSegment StartX=-64.7018 StartY=11 StartZ=0 EndX=-20.3 EndY=11 EndZ=0
    g1: LineSegment StartX=-20.3 StartY=11 StartZ=0 EndX=-20.3 EndY=7.1 EndZ=0
    g2: LineSegment StartX=-22.3 StartY=5.1 StartZ=0 EndX=-62.7018 EndY=5.1 EndZ=0
    g3: LineSegment StartX=-64.7018 StartY=7.1 StartZ=0 EndX=-64.7018 EndY=11 EndZ=0
    g4: ArcOfCircle CenterX=-62.7018 CenterY=7.1 CenterZ=0 NormalX=0 NormalY=0 NormalZ=1 AngleXU=0 Radius=2 StartAngle=3.14159 EndAngle=4.71239
    g5: ArcOfCircle CenterX=-22.3 CenterY=7.1 CenterZ=0 NormalX=0 NormalY=0 NormalZ=1 AngleXU=0 Radius=2 StartAngle=4.71239 EndAngle=6.28319
  constraints (14):
    c: Coincident(g0,g1)
    c: Coincident(g3,g0)
    c: Horizontal(g2)
    c: Vertical(g1)
    c: Vertical(g3)
    c: Coincident(g0,g-3)
    c: Coincident(g0,g-4)
    c: Tangent(g3,g4) = 1.5708
    c: Tangent(g2,g4) = 1.5708
    c: Tangent(g2,g5) = 1.5708
    c: Tangent(g1,g5) = 1.5708
    c: Equal(g4,g5)
    c: DistanceY(g2,g0) = 5.9
    c: Radius(g4) = 2
FEATURE [PartDesign::Pocket] Pocket009
  BaseFeature = -> Pocket008
  Length = 8
  Length2 = 100
  Profile = -> Sketch012
  Type = 0
FEATURE [PartDesign::Body] Body
  Group = -> [Sketch,Pad,Sketch001,Pad001,Sketch002,Pocket,Sketch003,Pocket001,Sketch004,Pocket002,Sketch005,Pocket003,Sketch006,Pad002,Sketch007,Pocket004,Sketch008,Pocket005,Sketch009,Pocket006,Sketch010,Pocket007,Sketch011,Pocket008,Sketch012,Pocket009]
  Origin = -> Origin
  Tip = -> Pocket009
FEATURE [Part::Fillet] Fillet
  Base = -> Pocket009
  Edges = 16 edges r=2: [Edge72,Edge86,Edge87,Edge172,Edge198,Edge199,Edge211,Edge216,Edge226,Edge235,Edge331,Edge347,Edge362,Edge375,Edge402,Edge411]
